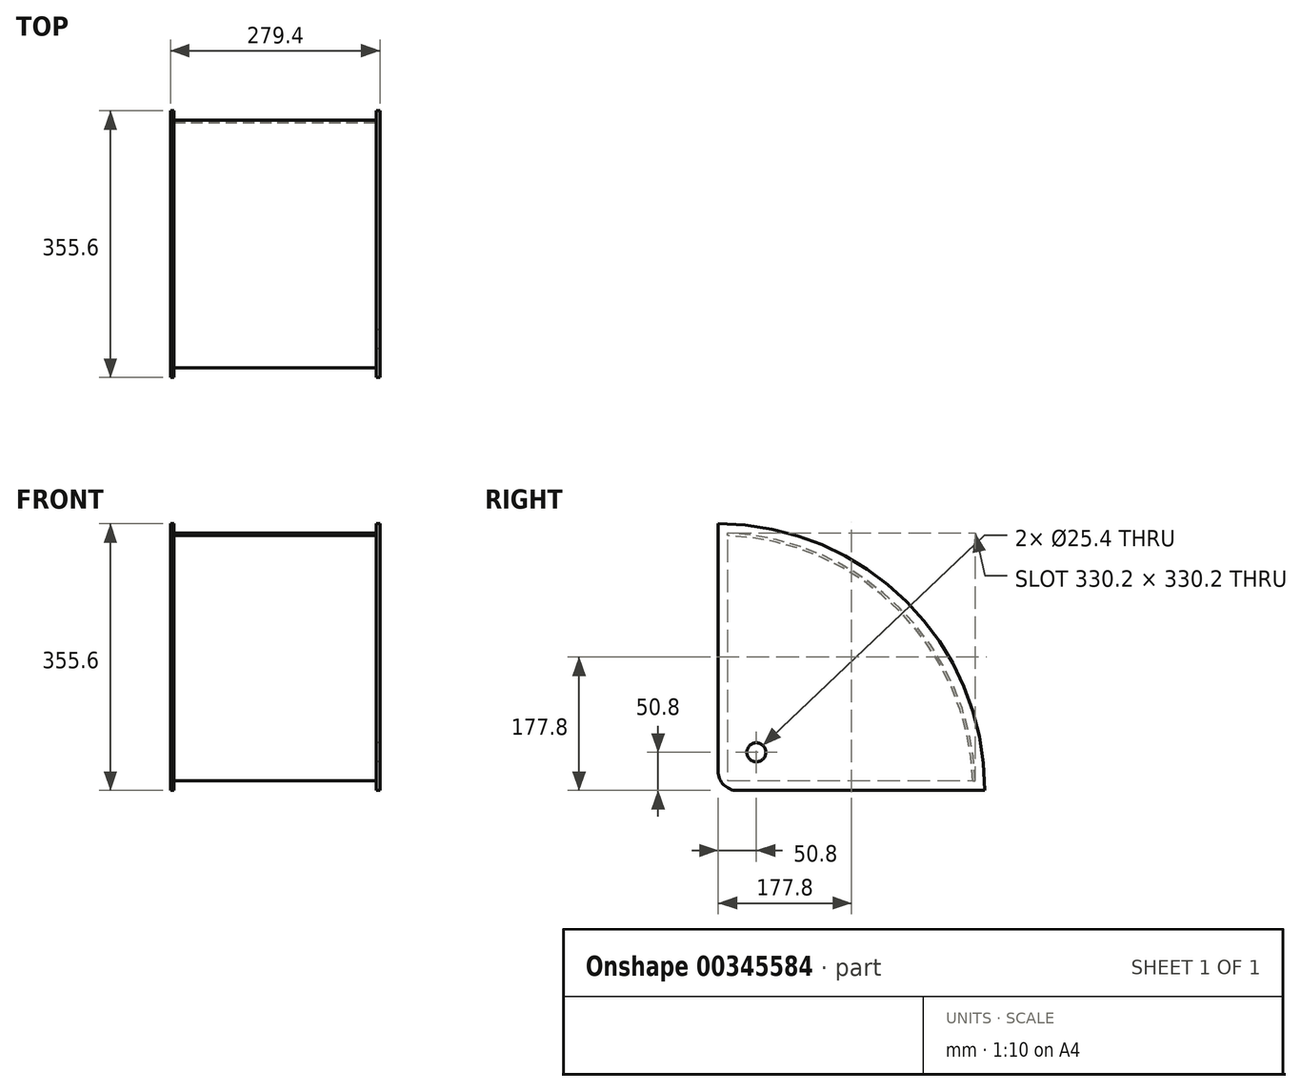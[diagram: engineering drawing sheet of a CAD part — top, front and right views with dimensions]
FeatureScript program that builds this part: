
annotation { "Feature Type Name" : "Feature", "Feature Type Description" : "" }
export const myFeature = defineFeature(function(context is Context, id is Id, definition is map)
    precondition{}
    {
        {
            var Q0;
            Q0=qCreatedBy(makeId("Right.planeOp"),FACE);
            var sketch = newSketch(context, id + "F0", { "sketchPlane" : qUnion([Q0])});
            skLineSegment(sketch, "E0", {"start": v(0, 355.6) * mm, "end": v(0, 0) * mm});
            skLineSegment(sketch, "E1", {"start": v(0, 0) * mm, "end": v(355.6, 0) * mm});
            skArc(sketch, "E2", {"start": v(0, 355.6) * mm, "mid": v(251.45, 251.45) * mm, "end": v(355.6, 0) * mm});
            skLineSegment(sketch, "E3", {"start": v(339.73, 12.7) * mm, "end": v(342.9, 12.7) * mm});
            skLineSegment(sketch, "E4", {"start": v(12.7, 339.73) * mm, "end": v(12.7, 342.9) * mm});
            skArc(sketch, "E5", {"start": v(12.7, 339.73) * mm, "mid": v(240.39, 240.39) * mm, "end": v(339.73, 12.7) * mm});
            skArc(sketch, "E6", {"start": v(342.9, 12.7) * mm, "mid": v(242.63, 242.63) * mm, "end": v(12.7, 342.9) * mm});
            skCircle(sketch, "E7", {"center": v(50.8, 50.8) * mm, "radius": 12.7 * mm});
            skSolve(sketch);
        }
        {
            var Q0;
            Q0=makeQuery(id+"F0.imprint","IMPRINT",FACE,{"disambiguationData":[TD([[makeQuery(id+"F0.imprint","IMPRINT",EDGE,{"derivedFrom":sQuery(id+"F0.wireOp",EDGE,"E0")}),1.0]])]});
            extrude(context, id + "F1", {"entities" : qUnion([Q0]), "depth" : 279.4 * mm, "symmetric" : true});
        }
        {
            var Q0;
            Q0=makeQuery(id+"F1.opExtrude","SWEPT_EDGE",EDGE,{"disambiguationData":[OSD([sQuery(id+"F0.wireOp",EDGE,"E0"),sQuery(id+"F0.wireOp",EDGE,"E1")])]});
            fillet(context, id + "F2", {"entities" : qUnion([Q0]), "radius" : 25.4 * mm, "tangentPropagation" : true, "allowEdgeOverflow" : false});
        }
        {
            var Q0;
            Q0 = qSketchRegion(id + "F0", true);
            extrude(context, id + "F3", {"entities" : qUnion([Q0]), "operationType" : NewBodyOperationType.REMOVE, "oppositeDirection" : true, "depth" : 269.88 * mm, "symmetric" : true});
        }
        {
            var Q0;
            Q0=makeQuery(id+"F0.imprint","IMPRINT",FACE,{"disambiguationData":[TD([[makeQuery(id+"F0.imprint","IMPRINT",EDGE,{"derivedFrom":sQuery(id+"F0.wireOp",EDGE,"E3")}),1.0]])]});
            var Q1;
            Q1=makeQuery(id+"F1.opExtrude","CAP_FACE",FACE,{"disambiguationData":[OSD([sQuery(id+"F0.wireOp",EDGE,"E0"),sQuery(id+"F0.wireOp",EDGE,"E1"),sQuery(id+"F0.wireOp",EDGE,"E2"),sQuery(id+"F0.wireOp",EDGE,"E3"),sQuery(id+"F0.wireOp",EDGE,"E4"),sQuery(id+"F0.wireOp",EDGE,"E5"),sQuery(id+"F0.wireOp",EDGE,"E6"),sQuery(id+"F0.wireOp",EDGE,"E7")])],"isStart":true});
            var Q2;
            Q2=makeQuery(id+"F1.opExtrude","CAP_FACE",FACE,{"disambiguationData":[OSD([sQuery(id+"F0.wireOp",EDGE,"E0"),sQuery(id+"F0.wireOp",EDGE,"E1"),sQuery(id+"F0.wireOp",EDGE,"E2"),sQuery(id+"F0.wireOp",EDGE,"E3"),sQuery(id+"F0.wireOp",EDGE,"E4"),sQuery(id+"F0.wireOp",EDGE,"E5"),sQuery(id+"F0.wireOp",EDGE,"E6"),sQuery(id+"F0.wireOp",EDGE,"E7")])],"isStart":false});
            extrude(context, id + "F4", {"entities" : qUnion([Q0]), "operationType" : NewBodyOperationType.ADD, "endBound" : BoundingType.UP_TO_SURFACE, "oppositeDirection" : true, "endBoundEntityFace" : qUnion([Q1]), "depth" : 25.4 * mm, "hasSecondDirection" : true, "secondDirectionBound" : BoundingType.UP_TO_SURFACE, "secondDirectionOppositeDirection" : false, "secondDirectionBoundEntityFace" : qUnion([Q2]), "secondDirectionDepth" : 25.4 * mm});
        }
    });
